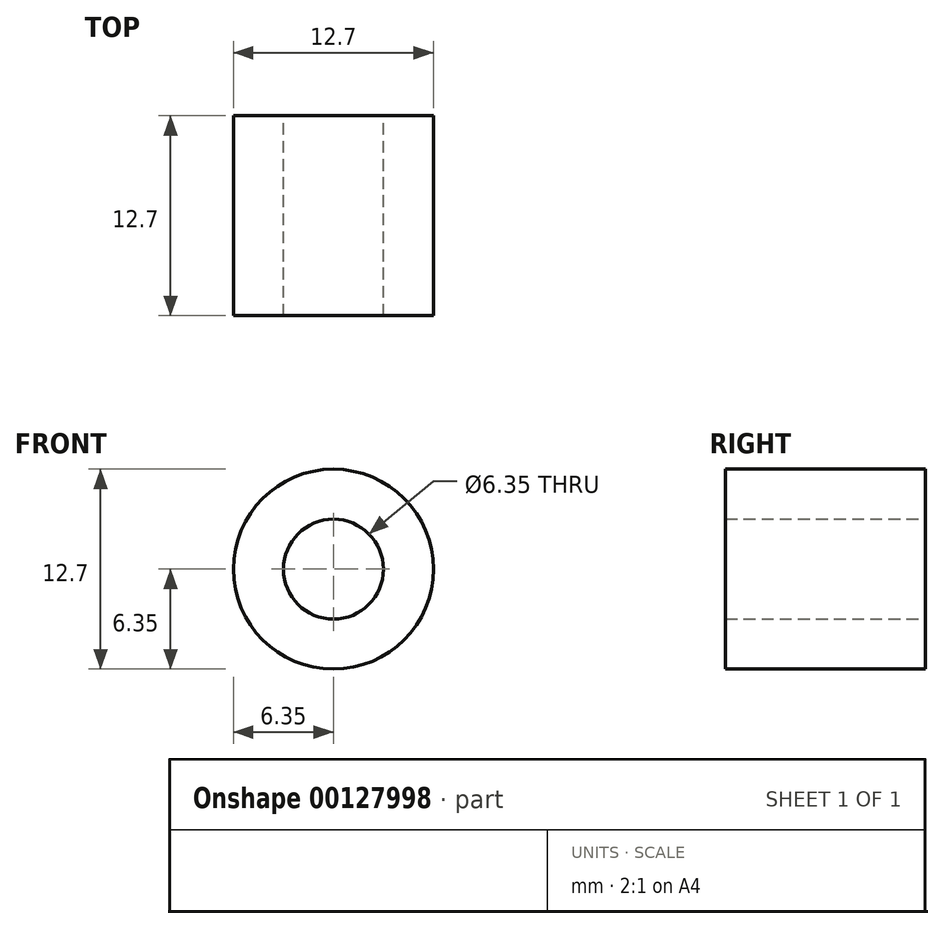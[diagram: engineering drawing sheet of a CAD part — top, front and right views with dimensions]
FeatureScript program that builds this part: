
annotation { "Feature Type Name" : "Feature", "Feature Type Description" : "" }
export const myFeature = defineFeature(function(context is Context, id is Id, definition is map)
    precondition{}
    {
        {
            var Q0;
            Q0=qCreatedBy(makeId("Front.planeOp"),FACE);
            var sketch = newSketch(context, id + "F0", { "sketchPlane" : qUnion([Q0])});
            skCircle(sketch, "E0", {"center": v(0, 0) * mm, "radius": 3.18 * mm});
            skCircle(sketch, "E1", {"center": v(0, 0) * mm, "radius": 6.35 * mm});
            skSolve(sketch);
        }
        {
            var Q0;
            Q0=makeQuery(id+"F0.imprint","IMPRINT",FACE,{"disambiguationData":[TD([[makeQuery(id+"F0.imprint","IMPRINT",EDGE,{"derivedFrom":sQuery(id+"F0.wireOp",EDGE,"E0")}),-1.0]])]});
            extrude(context, id + "F1", {"entities" : qUnion([Q0]), "depth" : 12.7 * mm});
        }
    });
